# Revit family: URA_Eclairage_de_Securite_Practice_Practice_Evolution
name_source: partatom
category: Luminaires
units: mm (PartAtom-declared; Revit-internal decimal feet)

## family parameters
Cote de connecteur circulaire = Utiliser le diamètre
Couper avec des vides une fois chargée = Non
Hôte = Face
Partagée = Non
Point de calcul de pièce = Non
Source d'éclairage = Oui
Type d'élément = Normal

## types (23) — shared parameters
Angle de l'inclinaison = 60.00°
CLASSE_DE_PROTECTION = II
CLASSE_DE_PROTECTION_(IP) = IP40
COULEUR_DU_BOITIER = blanc
Condition Générale d'Utilisation = https://export.legrand.com
DIAMETRE_EXTERNE = 187
DUREE_DE_GARANTIE_BAES_COMPLET = 4
Elévation par défaut = 1219 mm
Emettre à partir de la longueur de la ligne = 610 mm
Fichier de distribution photométrique = generic
Filtre de couleur = 16777215
Gradation des changements de température de couleur de lampe = <Aucun>
MATERIAU_DU_BOITIER = plastique
SOURCE_LUMINEUSE = LED non interchangeable

## per-type parameters (varying)
- BAES PRACTICE EVAC SUPER SATI: ADAPTE_AU_TYPE_DE_MARQUAGE=feuillet/plaque inséré(e); ALIMENTATION=décentralisé (batterie individuelle); CATEGORIE_PRODUIT=Autonome; DIAMETRE_D'ENCASTREMENT=152; DISTANCE_DE_RECONNAISSANCE=15; ETAT_DES_ACCUS=NiCd; FLUX_LUMINEUX_EN_MODE_D'URGENCE=45; FONCTION=Evac; FORMAT_PRODUIT=rond; HAUTEUR/PROFONDEUR=202; INSTALLATION_DE_SURVEILLANCE=auto-test automatique; LARGEUR=187; LARGEUR_DE_MONTAGE=152; LONGUEUR=240; LONGUEUR_D'ENCASTREMENT=152; MATERIAU_DU_COUVERCLE=plastique transparent; PROFONDEUR_D'ENCASTREMENT=61.5; PUISSANCE_DE_LA_LAMPE=0.5; REFERENCE_ARTICLE=119118; REF_BATTERIE_DE_RECHANGE=111906; RESERVE_DE_MARCHE=1; TENSION_NOMINALE_(MAX)=253; TENSION_NOMINALE_(MIN)=207; TYPE_DE_COMMUTATION=mode veille; TYPE_DE_MONTAGE=encastré; TYPE_DE_TENSION=CA
- BAES PRACTICE EVAC ADR: ADAPTE_AU_TYPE_DE_MARQUAGE=feuillet/plaque inséré(e); ALIMENTATION=décentralisé (batterie individuelle); CATEGORIE_PRODUIT=Autonome; DIAMETRE_D'ENCASTREMENT=152; DISTANCE_DE_RECONNAISSANCE=15; ETAT_DES_ACCUS=NiCd; FLUX_LUMINEUX_EN_MODE_D'URGENCE=45; FONCTION=Evac; FORMAT_PRODUIT=rond; HAUTEUR/PROFONDEUR=202; INSTALLATION_DE_SURVEILLANCE=auto-test automatique; LARGEUR=187; LARGEUR_DE_MONTAGE=152; LONGUEUR=240; LONGUEUR_D'ENCASTREMENT=152; MATERIAU_DU_COUVERCLE=plastique transparent; PROFONDEUR_D'ENCASTREMENT=61.5; PUISSANCE_DE_LA_LAMPE=0.5; REFERENCE_ARTICLE=119119; REF_BATTERIE_DE_RECHANGE=111906; RESERVE_DE_MARCHE=1; TENSION_NOMINALE_(MAX)=253; TENSION_NOMINALE_(MIN)=207; TYPE_DE_COMMUTATION=mode veille; TYPE_DE_MONTAGE=encastré; TYPE_DE_TENSION=CA
- BAES PRACTICE AMB SUPER SATI: ALIMENTATION=décentralisé (batterie individuelle); CATEGORIE_PRODUIT=Autonome; DIAMETRE_D'ENCASTREMENT=152; DISTANCE_DE_RECONNAISSANCE=15; ETAT_DES_ACCUS=NiMh; FLUX_LUMINEUX_EN_MODE_D'URGENCE=320; FONCTION=Amb; FORMAT_PRODUIT=rond; HAUTEUR/PROFONDEUR=75; INSTALLATION_DE_SURVEILLANCE=auto-test automatique; LARGEUR=187; LARGEUR_DE_MONTAGE=152; LONGUEUR=187; LONGUEUR_D'ENCASTREMENT=152; MATERIAU_DU_COUVERCLE=plastique transparent; PROFONDEUR_D'ENCASTREMENT=61.5; PUISSANCE_DE_LA_LAMPE=4; REFERENCE_ARTICLE=119128; REF_BATTERIE_DE_RECHANGE=2*111908; RESERVE_DE_MARCHE=1; TENSION_NOMINALE_(MAX)=253; TENSION_NOMINALE_(MIN)=207; TYPE_DE_COMMUTATION=mode veille; TYPE_DE_MONTAGE=encastré; TYPE_DE_TENSION=CA
- BAES PRACTICE AMBIANCE ADR: ALIMENTATION=décentralisé (batterie individuelle); CATEGORIE_PRODUIT=Autonome; DIAMETRE_D'ENCASTREMENT=152; DISTANCE_DE_RECONNAISSANCE=15; ETAT_DES_ACCUS=NiMh; FLUX_LUMINEUX_EN_MODE_D'URGENCE=320; FONCTION=Amb; FORMAT_PRODUIT=rond; HAUTEUR/PROFONDEUR=75; INSTALLATION_DE_SURVEILLANCE=auto-test automatique; LARGEUR=187; LARGEUR_DE_MONTAGE=152; LONGUEUR=187; LONGUEUR_D'ENCASTREMENT=152; MATERIAU_DU_COUVERCLE=plastique transparent; PROFONDEUR_D'ENCASTREMENT=61.5; PUISSANCE_DE_LA_LAMPE=4; REFERENCE_ARTICLE=119129; REF_BATTERIE_DE_RECHANGE=2*111908; RESERVE_DE_MARCHE=1; TENSION_NOMINALE_(MAX)=253; TENSION_NOMINALE_(MIN)=207; TYPE_DE_COMMUTATION=mode veille; TYPE_DE_MONTAGE=encastré; TYPE_DE_TENSION=CA
- PRACTICE habitation SUPER SATI: ADAPTE_AU_TYPE_DE_MARQUAGE=autocollant; ALIMENTATION=central (batterie centrale); CATEGORIE_PRODUIT=Autonome; ETAT_DES_ACCUS=NiCd; FLUX_LUMINEUX_EN_MODE_D'URGENCE=8; FONCTION=BAEH; FORMAT_PRODUIT=rectangle; HAUTEUR/PROFONDEUR=202; INSTALLATION_DE_SURVEILLANCE=auto-test automatique; LONGUEUR=240; MATERIAU_DU_COUVERCLE=verre transparent; PUISSANCE_DE_LA_LAMPE=0.8; REFERENCE_ARTICLE=119138; REF_BATTERIE_DE_RECHANGE=111906; RESERVE_DE_MARCHE=1; TENSION_NOMINALE_(MAX)=253; TENSION_NOMINALE_(MIN)=207; TYPE_DE_COMMUTATION=circuit permanent/circuit de secours; TYPE_DE_MONTAGE=montage en saillie au plafond; TYPE_DE_TENSION=CA
- PRACTICE DFM (BAES+BAEH) SUPER SATI: ADAPTE_AU_TYPE_DE_MARQUAGE=autocollant; ALIMENTATION=central (batterie centrale); CATEGORIE_PRODUIT=Autonome; ETAT_DES_ACCUS=NiCd; FLUX_LUMINEUX_EN_MODE_D'URGENCE=45; FONCTION=BAES+BAEH; FORMAT_PRODUIT=rectangle; HAUTEUR/PROFONDEUR=202; INSTALLATION_DE_SURVEILLANCE=auto-test automatique; LONGUEUR=240; MATERIAU_DU_COUVERCLE=verre transparent; PUISSANCE_DE_LA_LAMPE=4.5; REFERENCE_ARTICLE=119148; REF_BATTERIE_DE_RECHANGE=2*111906; RESERVE_DE_MARCHE=1; TENSION_NOMINALE_(MAX)=253; TENSION_NOMINALE_(MIN)=207; TYPE_DE_COMMUTATION=circuit permanent/circuit de secours; TYPE_DE_MONTAGE=montage en saillie au plafond; TYPE_DE_TENSION=CA
- PRACTICE DFM (BAES+BAEH) ADR: ADAPTE_AU_TYPE_DE_MARQUAGE=autocollant; ALIMENTATION=central (batterie centrale); CATEGORIE_PRODUIT=Autonome; ETAT_DES_ACCUS=NiCd; FLUX_LUMINEUX_EN_MODE_D'URGENCE=45; FONCTION=BAES+BAEH; FORMAT_PRODUIT=rectangle; HAUTEUR/PROFONDEUR=202; INSTALLATION_DE_SURVEILLANCE=auto-test automatique; LONGUEUR=240; MATERIAU_DU_COUVERCLE=verre transparent; PUISSANCE_DE_LA_LAMPE=4.5; REFERENCE_ARTICLE=119149; REF_BATTERIE_DE_RECHANGE=2*111906; RESERVE_DE_MARCHE=1; TENSION_NOMINALE_(MAX)=253; TENSION_NOMINALE_(MIN)=207; TYPE_DE_COMMUTATION=circuit permanent/circuit de secours; TYPE_DE_MONTAGE=montage en saillie au plafond; TYPE_DE_TENSION=CA
- BAES + DBR PRACTICE SATI: ADAPTE_AU_TYPE_DE_MARQUAGE=feuillet/plaque inséré(e); ALIMENTATION=décentralisé (batterie individuelle); CATEGORIE_PRODUIT=Autonome; DIAMETRE_D'ENCASTREMENT=152; DISTANCE_DE_RECONNAISSANCE=15; ETAT_DES_ACCUS=NiCd; FLUX_LUMINEUX_EN_MODE_D'URGENCE=45; FONCTION=DBR; FORMAT_PRODUIT=rond; HAUTEUR/PROFONDEUR=202; INSTALLATION_DE_SURVEILLANCE=auto-test automatique; LARGEUR=187; LARGEUR_DE_MONTAGE=152; LONGUEUR=240; LONGUEUR_D'ENCASTREMENT=152; MATERIAU_DU_COUVERCLE=plastique transparent; PROFONDEUR_D'ENCASTREMENT=61.5; PUISSANCE_DE_LA_LAMPE=1; REFERENCE_ARTICLE=119157; REF_BATTERIE_DE_RECHANGE=111901; RESERVE_DE_MARCHE=1; TENSION_NOMINALE_(MAX)=253; TENSION_NOMINALE_(MIN)=207; TYPE_DE_COMMUTATION=mode veille; TYPE_DE_MONTAGE=encastré; TYPE_DE_TENSION=CA
- BAES + DBR PRACTICE ADR: ADAPTE_AU_TYPE_DE_MARQUAGE=feuillet/plaque inséré(e); ALIMENTATION=décentralisé (batterie individuelle); CATEGORIE_PRODUIT=Autonome; DIAMETRE_D'ENCASTREMENT=152; DISTANCE_DE_RECONNAISSANCE=15; ETAT_DES_ACCUS=NiCd; FLUX_LUMINEUX_EN_MODE_D'URGENCE=45; FONCTION=DBR; FORMAT_PRODUIT=rond; HAUTEUR/PROFONDEUR=202; INSTALLATION_DE_SURVEILLANCE=auto-test automatique; LARGEUR=187; LARGEUR_DE_MONTAGE=152; LONGUEUR=240; LONGUEUR_D'ENCASTREMENT=152; MATERIAU_DU_COUVERCLE=plastique transparent; PROFONDEUR_D'ENCASTREMENT=61.5; PUISSANCE_DE_LA_LAMPE=1; REFERENCE_ARTICLE=119159; REF_BATTERIE_DE_RECHANGE=111901; RESERVE_DE_MARCHE=1; TENSION_NOMINALE_(MAX)=253; TENSION_NOMINALE_(MIN)=207; TYPE_DE_COMMUTATION=mode veille; TYPE_DE_MONTAGE=encastré; TYPE_DE_TENSION=CA
- BAES PRACTICE EVO EVAC S.SATI: ADAPTE_AU_TYPE_DE_MARQUAGE=plaque en verre acrylique; ALIMENTATION=décentralisé (batterie individuelle); CATEGORIE_PRODUIT=Autonome; DIAMETRE_D'ENCASTREMENT=152; DISTANCE_DE_RECONNAISSANCE=15; ETAT_DES_ACCUS=NiCd; FLUX_LUMINEUX_EN_MODE_D'URGENCE=45; FONCTION=Evac; FORMAT_PRODUIT=rond; HAUTEUR/PROFONDEUR=75; INSTALLATION_DE_SURVEILLANCE=auto-test automatique; LARGEUR=187; LARGEUR_DE_MONTAGE=152; LONGUEUR=187; LONGUEUR_D'ENCASTREMENT=152; MATERIAU_DU_COUVERCLE=plastique transparent; PROFONDEUR_D'ENCASTREMENT=61.5; PUISSANCE_DE_LA_LAMPE=0.5; REFERENCE_ARTICLE=119818; REF_BATTERIE_DE_RECHANGE=111906; RESERVE_DE_MARCHE=1; TENSION_NOMINALE_(MAX)=253; TENSION_NOMINALE_(MIN)=207; TYPE_DE_COMMUTATION=mode veille; TYPE_DE_MONTAGE=encastré; TYPE_DE_TENSION=CA
- BAES PRACTICE EVO EVAC ADR: ADAPTE_AU_TYPE_DE_MARQUAGE=plaque en verre acrylique; ALIMENTATION=décentralisé (batterie individuelle); CATEGORIE_PRODUIT=Autonome; DIAMETRE_D'ENCASTREMENT=152; DISTANCE_DE_RECONNAISSANCE=15; ETAT_DES_ACCUS=NiCd; FLUX_LUMINEUX_EN_MODE_D'URGENCE=45; FONCTION=Evac; FORMAT_PRODUIT=rond; HAUTEUR/PROFONDEUR=75; INSTALLATION_DE_SURVEILLANCE=auto-test automatique; LARGEUR=187; LARGEUR_DE_MONTAGE=152; LONGUEUR=187; LONGUEUR_D'ENCASTREMENT=152; MATERIAU_DU_COUVERCLE=plastique transparent; PROFONDEUR_D'ENCASTREMENT=61.5; PUISSANCE_DE_LA_LAMPE=0.5; REFERENCE_ARTICLE=119819; REF_BATTERIE_DE_RECHANGE=111906; RESERVE_DE_MARCHE=1; TENSION_NOMINALE_(MAX)=253; TENSION_NOMINALE_(MIN)=207; TYPE_DE_COMMUTATION=mode veille; TYPE_DE_MONTAGE=encastré; TYPE_DE_TENSION=CA
- BAES PRACTICE EVO AMB S.SATI: ALIMENTATION=décentralisé (batterie individuelle); CATEGORIE_PRODUIT=Autonome; DIAMETRE_D'ENCASTREMENT=152; DISTANCE_DE_RECONNAISSANCE=15; ETAT_DES_ACCUS=NiMh; FLUX_LUMINEUX_EN_MODE_D'URGENCE=320; FONCTION=Amb; FORMAT_PRODUIT=rond; HAUTEUR/PROFONDEUR=75; INSTALLATION_DE_SURVEILLANCE=auto-test automatique; LARGEUR=187; LARGEUR_DE_MONTAGE=152; LONGUEUR=187; LONGUEUR_D'ENCASTREMENT=152; MATERIAU_DU_COUVERCLE=plastique transparent; PROFONDEUR_D'ENCASTREMENT=61.5; PUISSANCE_DE_LA_LAMPE=4; REFERENCE_ARTICLE=119828; REF_BATTERIE_DE_RECHANGE=2*111908; RESERVE_DE_MARCHE=1; TENSION_NOMINALE_(MAX)=253; TENSION_NOMINALE_(MIN)=207; TYPE_DE_COMMUTATION=mode veille; TYPE_DE_MONTAGE=encastré; TYPE_DE_TENSION=CA
- PRACTICE EVOLUTION habitation SUPER SATI: ADAPTE_AU_TYPE_DE_MARQUAGE=autocollant; ALIMENTATION=central (batterie centrale); CATEGORIE_PRODUIT=Autonome; ETAT_DES_ACCUS=NiCd; FLUX_LUMINEUX_EN_MODE_D'URGENCE=8; FONCTION=BAEH; FORMAT_PRODUIT=rectangle; HAUTEUR/PROFONDEUR=202; INSTALLATION_DE_SURVEILLANCE=auto-test automatique; LONGUEUR=240; MATERIAU_DU_COUVERCLE=verre transparent; PUISSANCE_DE_LA_LAMPE=0.8; REFERENCE_ARTICLE=119838; REF_BATTERIE_DE_RECHANGE=111906; RESERVE_DE_MARCHE=1; TENSION_NOMINALE_(MAX)=253; TENSION_NOMINALE_(MIN)=207; TYPE_DE_COMMUTATION=circuit permanent/circuit de secours; TYPE_DE_MONTAGE=montage en saillie au plafond; TYPE_DE_TENSION=CA
- PRACTICE EVOLUTION DFM (BAES+BAEH) SUPER SATI: ADAPTE_AU_TYPE_DE_MARQUAGE=autocollant; ALIMENTATION=central (batterie centrale); CATEGORIE_PRODUIT=Autonome; ETAT_DES_ACCUS=NiCd; FLUX_LUMINEUX_EN_MODE_D'URGENCE=45; FONCTION=BAES+BAEH; FORMAT_PRODUIT=rectangle; HAUTEUR/PROFONDEUR=202; INSTALLATION_DE_SURVEILLANCE=auto-test automatique; LONGUEUR=240; MATERIAU_DU_COUVERCLE=verre transparent; PUISSANCE_DE_LA_LAMPE=4.5; REFERENCE_ARTICLE=119848; REF_BATTERIE_DE_RECHANGE=2*111906; RESERVE_DE_MARCHE=1; TENSION_NOMINALE_(MAX)=253; TENSION_NOMINALE_(MIN)=207; TYPE_DE_COMMUTATION=circuit permanent/circuit de secours; TYPE_DE_MONTAGE=montage en saillie au plafond; TYPE_DE_TENSION=CA
- BAES + BAEH PRACTICE EV S.SATI: ADAPTE_AU_TYPE_DE_MARQUAGE=plaque en verre acrylique; ALIMENTATION=décentralisé (batterie individuelle); CATEGORIE_PRODUIT=Autonome; DIAMETRE_D'ENCASTREMENT=152; DISTANCE_DE_RECONNAISSANCE=15; ETAT_DES_ACCUS=NiCd; FLUX_LUMINEUX_EN_MODE_D'URGENCE=45; FONCTION=DBR; FORMAT_PRODUIT=rond; HAUTEUR/PROFONDEUR=75; INSTALLATION_DE_SURVEILLANCE=auto-test automatique; LARGEUR=187; LARGEUR_DE_MONTAGE=152; LONGUEUR=187; LONGUEUR_D'ENCASTREMENT=152; MATERIAU_DU_COUVERCLE=plastique transparent; PROFONDEUR_D'ENCASTREMENT=61.5; PUISSANCE_DE_LA_LAMPE=1; REFERENCE_ARTICLE=119857; REF_BATTERIE_DE_RECHANGE=111901; RESERVE_DE_MARCHE=1; TENSION_NOMINALE_(MAX)=253; TENSION_NOMINALE_(MIN)=207; TYPE_DE_COMMUTATION=mode veille; TYPE_DE_MONTAGE=encastré; TYPE_DE_TENSION=CA
- BAES + DBR PRACTICE EVO SATI: ADAPTE_AU_TYPE_DE_MARQUAGE=feuillet/plaque inséré(e); ALIMENTATION=central (batterie centrale); CATEGORIE_PRODUIT=LSC; DIAMETRE_D'ENCASTREMENT=152; DISTANCE_DE_RECONNAISSANCE=15; ETAT_DES_ACCUS=non applicable; FLUX_LUMINEUX_EN_MODE_D'URGENCE=45; FONCTION=Evac; FORMAT_PRODUIT=rond; HAUTEUR/PROFONDEUR=202; INSTALLATION_DE_SURVEILLANCE=auto-test automatique; LARGEUR=187; LARGEUR_DE_MONTAGE=152; LONGUEUR=240; LONGUEUR_D'ENCASTREMENT=152; MATERIAU_DU_COUVERCLE=plastique transparent; PROFONDEUR_D'ENCASTREMENT=61.5; PUISSANCE_DE_LA_LAMPE=1; REFERENCE_ARTICLE=129114; TENSION_NOMINALE_(MAX)=230; TENSION_NOMINALE_(MIN)=110; TYPE_DE_COMMUTATION=circuit permanent/circuit de secours; TYPE_DE_MONTAGE=encastré; TYPE_DE_TENSION=CA/CC
- LSC PRACTICE EVAC 110/220/230: ADAPTE_AU_TYPE_DE_MARQUAGE=feuillet/plaque inséré(e); ALIMENTATION=central (batterie centrale); CATEGORIE_PRODUIT=LSC; DIAMETRE_D'ENCASTREMENT=152; DISTANCE_DE_RECONNAISSANCE=15; ETAT_DES_ACCUS=non applicable; FLUX_LUMINEUX_EN_MODE_D'URGENCE=45; FONCTION=Amb; FORMAT_PRODUIT=rond; HAUTEUR/PROFONDEUR=202; INSTALLATION_DE_SURVEILLANCE=auto-test automatique; LARGEUR=187; LARGEUR_DE_MONTAGE=152; LONGUEUR=240; LONGUEUR_D'ENCASTREMENT=152; MATERIAU_DU_COUVERCLE=plastique transparent; PROFONDEUR_D'ENCASTREMENT=61.5; PUISSANCE_DE_LA_LAMPE=1; REFERENCE_ARTICLE=129115; TENSION_NOMINALE_(MAX)=48; TENSION_NOMINALE_(MIN)=24; TYPE_DE_COMMUTATION=circuit permanent/circuit de secours; TYPE_DE_MONTAGE=encastré; TYPE_DE_TENSION=CC
- LSC PRACTICE EVACUATION 24/48: ALIMENTATION=central (batterie centrale); CATEGORIE_PRODUIT=LSC; DIAMETRE_D'ENCASTREMENT=152; DISTANCE_DE_RECONNAISSANCE=15; ETAT_DES_ACCUS=non applicable; FLUX_LUMINEUX_EN_MODE_D'URGENCE=320; FONCTION=Amb; FORMAT_PRODUIT=rond; HAUTEUR/PROFONDEUR=75; INSTALLATION_DE_SURVEILLANCE=auto-test automatique; LARGEUR=187; LARGEUR_DE_MONTAGE=152; LONGUEUR=187; LONGUEUR_D'ENCASTREMENT=152; MATERIAU_DU_COUVERCLE=plastique transparent; PROFONDEUR_D'ENCASTREMENT=61.5; PUISSANCE_DE_LA_LAMPE=4; REFERENCE_ARTICLE=129124; TENSION_NOMINALE_(MAX)=230; TENSION_NOMINALE_(MIN)=110; TYPE_DE_COMMUTATION=circuit permanent/circuit de secours; TYPE_DE_MONTAGE=encastré; TYPE_DE_TENSION=CA/CC
- LSC PRACTICE AMB 110/220/230: ALIMENTATION=central (batterie centrale); CATEGORIE_PRODUIT=LSC; DIAMETRE_D'ENCASTREMENT=152; DISTANCE_DE_RECONNAISSANCE=15; ETAT_DES_ACCUS=non applicable; FLUX_LUMINEUX_EN_MODE_D'URGENCE=320; FONCTION=Amb; FORMAT_PRODUIT=rond; HAUTEUR/PROFONDEUR=75; INSTALLATION_DE_SURVEILLANCE=auto-test automatique; LARGEUR=187; LARGEUR_DE_MONTAGE=152; LONGUEUR=187; LONGUEUR_D'ENCASTREMENT=152; MATERIAU_DU_COUVERCLE=plastique transparent; PROFONDEUR_D'ENCASTREMENT=61.5; PUISSANCE_DE_LA_LAMPE=4; REFERENCE_ARTICLE=129125; TENSION_NOMINALE_(MAX)=48; TENSION_NOMINALE_(MIN)=24; TYPE_DE_COMMUTATION=circuit permanent/circuit de secours; TYPE_DE_MONTAGE=encastré; TYPE_DE_TENSION=CC
- LSC PRACTICE AMBIANCE 24/48: ADAPTE_AU_TYPE_DE_MARQUAGE=plaque en verre acrylique; ALIMENTATION=central (batterie centrale); CATEGORIE_PRODUIT=LSC; DIAMETRE_D'ENCASTREMENT=152; DISTANCE_DE_RECONNAISSANCE=15; ETAT_DES_ACCUS=non applicable; FLUX_LUMINEUX_EN_MODE_D'URGENCE=45; FONCTION=Evac; FORMAT_PRODUIT=rond; HAUTEUR/PROFONDEUR=75; INSTALLATION_DE_SURVEILLANCE=auto-test automatique; LARGEUR=187; LARGEUR_DE_MONTAGE=152; LONGUEUR=187; LONGUEUR_D'ENCASTREMENT=152; MATERIAU_DU_COUVERCLE=plastique transparent; PROFONDEUR_D'ENCASTREMENT=61.5; PUISSANCE_DE_LA_LAMPE=1; REFERENCE_ARTICLE=129814; TENSION_NOMINALE_(MAX)=230; TENSION_NOMINALE_(MIN)=110; TYPE_DE_COMMUTATION=circuit permanent/circuit de secours; TYPE_DE_MONTAGE=encastré; TYPE_DE_TENSION=CA/CC
- LSC PRACTICE EVO EVAC 110/230: ALIMENTATION=central (batterie centrale); CATEGORIE_PRODUIT=LSC; ETAT_DES_ACCUS=non applicable; FLUX_LUMINEUX_EN_MODE_D'URGENCE=45; FONCTION=Evac; FORMAT_PRODUIT=rectangle; HAUTEUR/PROFONDEUR=202; INSTALLATION_DE_SURVEILLANCE=sans; LONGUEUR=240; MATERIAU_DU_COUVERCLE=plastique structuré; PUISSANCE_DE_LA_LAMPE=4.5; REFERENCE_ARTICLE=129815; RESERVE_DE_MARCHE=1; TENSION_NOMINALE_(MAX)=48; TENSION_NOMINALE_(MIN)=24; TYPE_DE_COMMUTATION=circuit permanent/circuit de secours; TYPE_DE_MONTAGE=montage en saillie au plafond; TYPE_DE_TENSION=CC
- LSC PRACTICE EVOLUTION ambiance 110/220 VDC et 230 VAC: ALIMENTATION=central (batterie centrale); CATEGORIE_PRODUIT=LSC; ETAT_DES_ACCUS=non applicable; FLUX_LUMINEUX_EN_MODE_D'URGENCE=320; FONCTION=Amb; FORMAT_PRODUIT=rectangle; HAUTEUR/PROFONDEUR=202; INSTALLATION_DE_SURVEILLANCE=sans; LONGUEUR=240; MATERIAU_DU_COUVERCLE=plastique structuré; PUISSANCE_DE_LA_LAMPE=32; REFERENCE_ARTICLE=129824; RESERVE_DE_MARCHE=1; TENSION_NOMINALE_(MAX)=253; TENSION_NOMINALE_(MIN)=207; TYPE_DE_COMMUTATION=circuit permanent/circuit de secours; TYPE_DE_MONTAGE=montage en saillie au plafond; TYPE_DE_TENSION=CA
- LSC PRACTICE EVOLUTION ambiance 24/48 VDC: ALIMENTATION=central (batterie centrale); CATEGORIE_PRODUIT=LSC; ETAT_DES_ACCUS=non applicable; FLUX_LUMINEUX_EN_MODE_D'URGENCE=320; FONCTION=Amb; FORMAT_PRODUIT=rectangle; HAUTEUR/PROFONDEUR=202; INSTALLATION_DE_SURVEILLANCE=sans; LONGUEUR=240; MATERIAU_DU_COUVERCLE=plastique structuré; PUISSANCE_DE_LA_LAMPE=32; REFERENCE_ARTICLE=129825; RESERVE_DE_MARCHE=1; TENSION_NOMINALE_(MAX)=48; TENSION_NOMINALE_(MIN)=24; TYPE_DE_COMMUTATION=circuit permanent/circuit de secours; TYPE_DE_MONTAGE=montage en saillie au plafond; TYPE_DE_TENSION=CC

note: column(s) folded — value = type name in every type: DESIGNATION_ARTICLE
